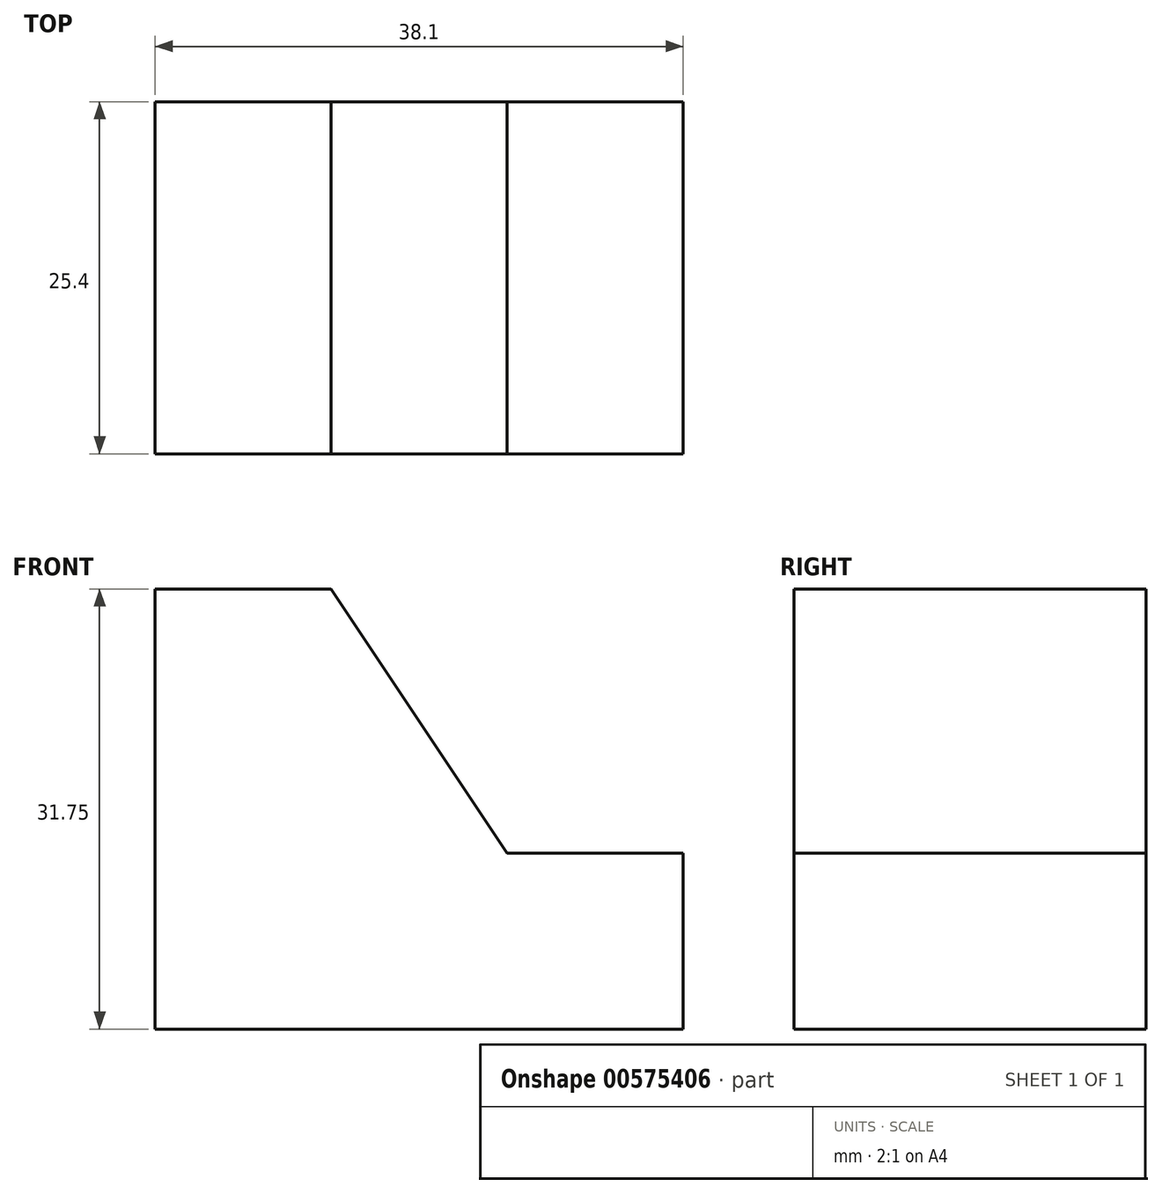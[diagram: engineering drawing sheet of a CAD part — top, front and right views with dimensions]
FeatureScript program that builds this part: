
annotation { "Feature Type Name" : "Feature", "Feature Type Description" : "" }
export const myFeature = defineFeature(function(context is Context, id is Id, definition is map)
    precondition{}
    {
        {
            var Q0;
            Q0=qCreatedBy(makeId("Front.planeOp"),FACE);
            var sketch = newSketch(context, id + "F0", { "sketchPlane" : qUnion([Q0])});
            skLineSegment(sketch, "E0", {"start": v(0, 0) * mm, "end": v(38.1, 0) * mm});
            skLineSegment(sketch, "E1", {"start": v(38.1, 0) * mm, "end": v(38.1, 31.75) * mm});
            skLineSegment(sketch, "E2", {"start": v(38.1, 31.75) * mm, "end": v(0, 31.75) * mm});
            skLineSegment(sketch, "E3", {"start": v(0, 31.75) * mm, "end": v(0, 0) * mm});
            skSolve(sketch);
        }
        {
            var Q0;
            Q0=makeQuery(id+"F0.imprint","IMPRINT",FACE,{"disambiguationData":[TD([[makeQuery(id+"F0.imprint","IMPRINT",EDGE,{"derivedFrom":sQuery(id+"F0.wireOp",EDGE,"E0")}),1.0]])]});
            extrude(context, id + "F1", {"entities" : qUnion([Q0]), "depth" : 25.4 * mm, "offsetDistance" : 25.4 * mm});
        }
        {
            var Q0;
            Q0=makeQuery(id+"F1.opExtrude","CAP_FACE",FACE,{"disambiguationData":[OSD([sQuery(id+"F0.wireOp",EDGE,"E0"),sQuery(id+"F0.wireOp",EDGE,"E1"),sQuery(id+"F0.wireOp",EDGE,"E2"),sQuery(id+"F0.wireOp",EDGE,"E3")])],"isStart":false});
            var sketch = newSketch(context, id + "F2", { "sketchPlane" : qUnion([Q0])});
            skLineSegment(sketch, "E4", {"start": v(38.1, 0) * mm, "end": v(25.4, 0) * mm});
            skLineSegment(sketch, "E5", {"start": v(38.1, 0) * mm, "end": v(38.1, 12.7) * mm});
            skLineSegment(sketch, "E6", {"start": v(38.1, 12.7) * mm, "end": v(25.4, 12.7) * mm});
            skLineSegment(sketch, "E7", {"start": v(25.4, 12.7) * mm, "end": v(25.4, 0) * mm});
            skLineSegment(sketch, "E8", {"start": v(0, 31.75) * mm, "end": v(12.7, 31.75) * mm});
            skLineSegment(sketch, "E9", {"start": v(12.7, 31.75) * mm, "end": v(25.4, 12.7) * mm});
            skSolve(sketch);
        }
        {
            var Q0;
            {var subQ0=sQuery(id+"F2.wireOp",EDGE,"E6");Q0=makeQuery(id+"F2.imprint","IMPRINT",FACE,{"disambiguationData":[TD([[makeQuery(id+"F2.imprint","IMPRINT",EDGE,{"derivedFrom":subQ0}),-1.0]])]});}
            extrude(context, id + "F3", {"entities" : qUnion([Q0]), "operationType" : NewBodyOperationType.REMOVE, "oppositeDirection" : true, "depth" : 25.4 * mm, "offsetDistance" : 25.4 * mm});
        }
    });
